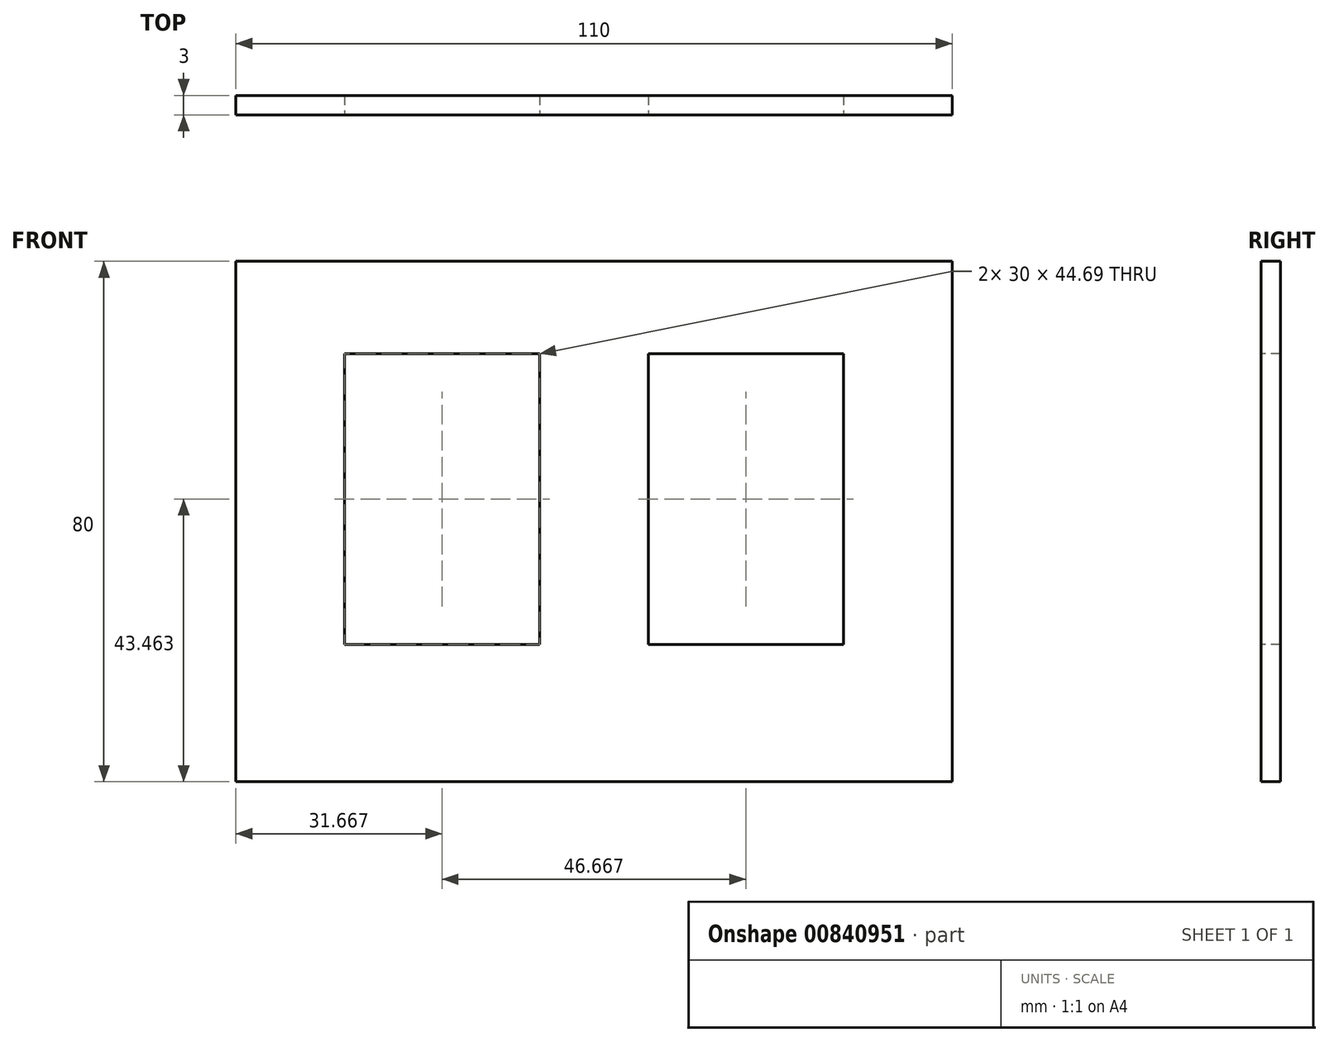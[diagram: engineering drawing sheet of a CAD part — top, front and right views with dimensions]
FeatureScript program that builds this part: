
annotation { "Feature Type Name" : "Feature", "Feature Type Description" : "" }
export const myFeature = defineFeature(function(context is Context, id is Id, definition is map)
    precondition{}
    {
        {
            var Q0;
            Q0=qCreatedBy(makeId("Front.planeOp"),FACE);
            var sketch = newSketch(context, id + "F0", { "sketchPlane" : qUnion([Q0])});
            skLineSegment(sketch, "E0.bottom", {"start": v(0, 0) * mm, "end": v(110, 0) * mm});
            skLineSegment(sketch, "E0.top", {"start": v(0, 80) * mm, "end": v(110, 80) * mm});
            skLineSegment(sketch, "E0.left", {"start": v(0, 0) * mm, "end": v(0, 80) * mm});
            skLineSegment(sketch, "E0.right", {"start": v(110, 0) * mm, "end": v(110, 80) * mm});
            skSolve(sketch);
        }
        {
            var Q0;
            Q0 = qSketchRegion(id + "F0", true);
            extrude(context, id + "F1", {"entities" : qUnion([Q0]), "depth" : 3 * mm, "offsetDistance" : 25 * mm});
        }
        {
            var Q0;
            Q0=makeQuery(id+"F1.opExtrude","CAP_FACE",FACE,{"disambiguationData":[OSD([sQuery(id+"F0.wireOp",EDGE,"E0.bottom"),sQuery(id+"F0.wireOp",EDGE,"E0.top"),sQuery(id+"F0.wireOp",EDGE,"E0.left"),sQuery(id+"F0.wireOp",EDGE,"E0.right")])],"isStart":false});
            var sketch = newSketch(context, id + "F2", { "sketchPlane" : qUnion([Q0])});
            skLineSegment(sketch, "E1.bottom", {"start": v(16.67, 65.8) * mm, "end": v(46.67, 65.8) * mm});
            skLineSegment(sketch, "E1.top", {"start": v(16.67, 21.12) * mm, "end": v(46.67, 21.12) * mm});
            skLineSegment(sketch, "E1.left", {"start": v(16.67, 65.8) * mm, "end": v(16.67, 21.12) * mm});
            skLineSegment(sketch, "E1.right", {"start": v(46.67, 65.8) * mm, "end": v(46.67, 21.12) * mm});
            skLineSegment(sketch, "E2.1.0.0", {"start": v(63.33, 65.8) * mm, "end": v(93.33, 65.8) * mm});
            skLineSegment(sketch, "E2.1.0.1", {"start": v(63.33, 65.8) * mm, "end": v(63.33, 21.12) * mm});
            skLineSegment(sketch, "E2.1.0.2", {"start": v(93.33, 65.8) * mm, "end": v(93.33, 21.12) * mm});
            skLineSegment(sketch, "E2.1.0.3", {"start": v(63.33, 21.12) * mm, "end": v(93.33, 21.12) * mm});
            skLineSegment(sketch, "E2.direction1", {"start": v(16.67, 65.8) * mm, "end": v(63.33, 65.8) * mm, "construction": true});
            skSolve(sketch);
        }
        {
            var Q0;
            Q0 = qSketchRegion(id + "F2", true);
            extrude(context, id + "F3", {"entities" : qUnion([Q0]), "operationType" : NewBodyOperationType.REMOVE, "oppositeDirection" : true, "depth" : 25 * mm, "offsetDistance" : 25 * mm});
        }
    });
